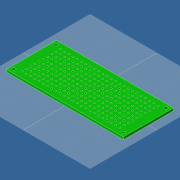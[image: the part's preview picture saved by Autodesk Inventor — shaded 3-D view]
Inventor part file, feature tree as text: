
AUTODESK INVENTOR PART (.ipt)
format: ipt  version: 2016 SP2 (Build 200236200, 236)  size: 322,560 bytes
history: native  units: mm
features: sketch x2, extrude x2, hole x1
ambient origin geometry x8: Origin, YZ Plane, XZ Plane, XY Plane, X Axis, Y Axis, Z Axis, Center Point
bodies: Volumenkörper1 (feature_tree)
feature tree (5):
  sketch  "Skizze1"  dims[d0=70.0mm d1=30.0mm]
  extrude  "Extrusion1"  Depth=30.0mm
  hole  "Bohrung1"  [1 undecoded]
  extrude  "Extrusion2"  Depth=1.5mm
  sketch  "Skizze2"  dims[d2=1.5mm d3=0.0mm d4=2.54mm d5=2.54mm d6=50.0mm d8=2.54mm d9=120.0mm d11=2.54mm d14=120.0mm d16=2.54mm d17=50.0mm d19=2.54mm d22=50.0mm d24=2.54mm d25=120.0mm d27=2.54mm d30=50.0mm d32=2.54mm d33=120.0mm d35=2.54mm d38=1.0mm d39=6.0mm d40=4.0mm d41=2.0mm d42=90.0deg d43=8.0mm d44=20.594885mm d45=2.0mm d46=65.5mm d47=25.5mm d48=1.5mm d49=0.0mm]
note: 1 required parameter value undecoded (feature->parameter linkage not recoverable at this tier; creation-order binding heuristic only, values carry confidence <= 0.55)
